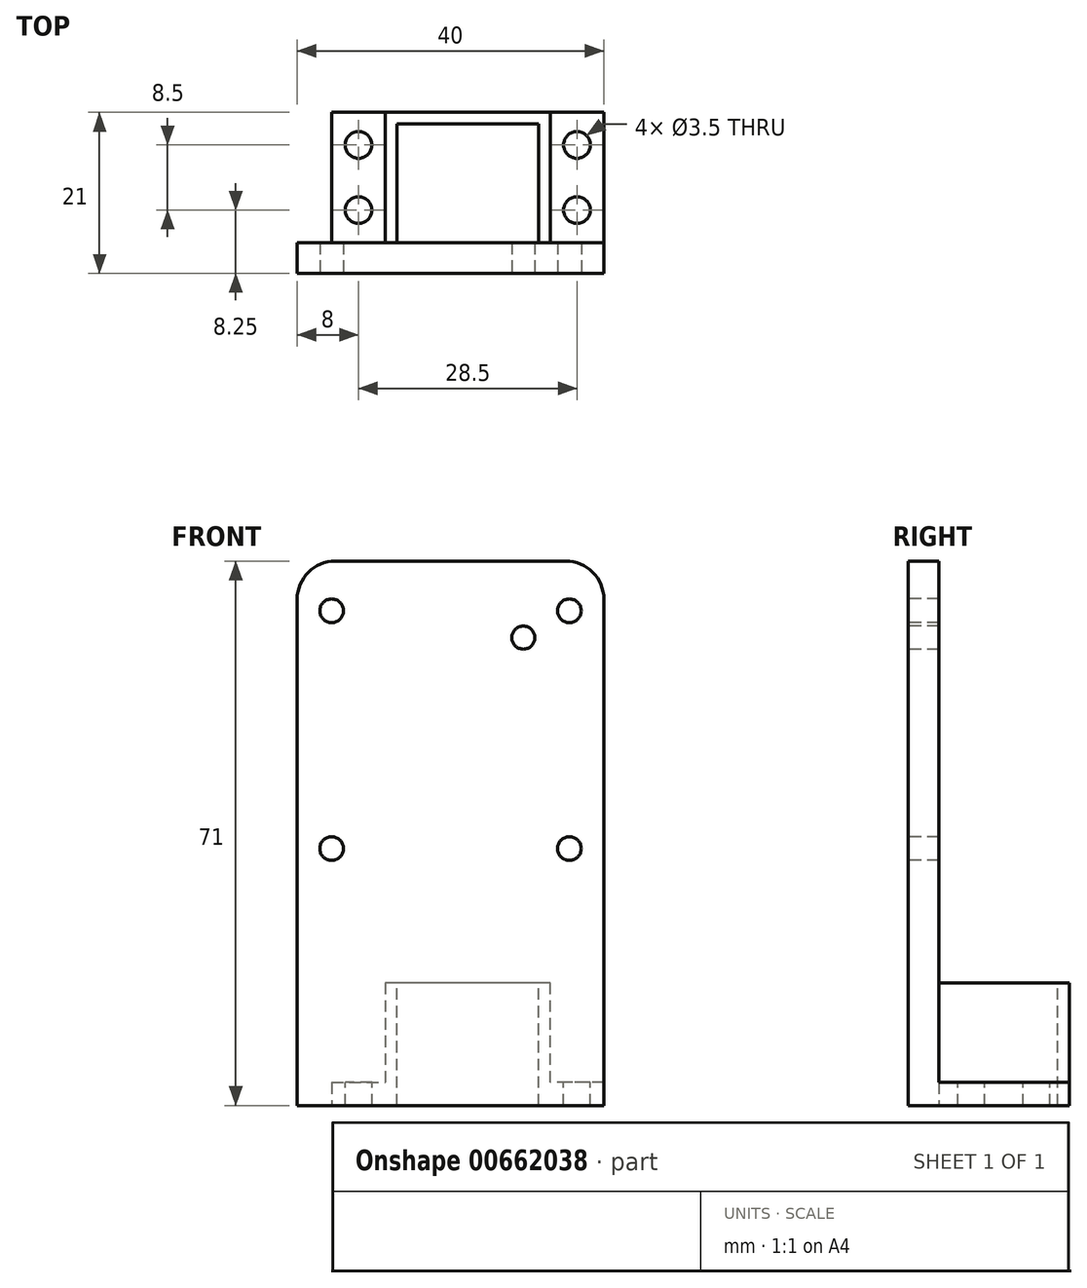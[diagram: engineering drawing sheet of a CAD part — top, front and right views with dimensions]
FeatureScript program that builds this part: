
annotation { "Feature Type Name" : "Feature", "Feature Type Description" : "" }
export const myFeature = defineFeature(function(context is Context, id is Id, definition is map)
    precondition{}
    {
        {
            var Q0;
            Q0=qCreatedBy(makeId("Front.planeOp"),FACE);
            var sketch = newSketch(context, id + "F0", { "sketchPlane" : qUnion([Q0])});
            skLineSegment(sketch, "E0.bottom", {"start": v(-20, 35.5) * mm, "end": v(20, 35.5) * mm});
            skLineSegment(sketch, "E0.top", {"start": v(-20, -35.5) * mm, "end": v(20, -35.5) * mm});
            skLineSegment(sketch, "E0.left", {"start": v(-20, 35.5) * mm, "end": v(-20, -35.5) * mm});
            skLineSegment(sketch, "E0.right", {"start": v(20, 35.5) * mm, "end": v(20, -35.5) * mm});
            skPoint(sketch, "E0.middle", {"position": v(0, 0) * mm});
            skSolve(sketch);
        }
        {
            var Q0;
            Q0 = qSketchRegion(id + "F0", true);
            extrude(context, id + "F1", {"entities" : qUnion([Q0]), "depth" : 4 * mm, "offsetDistance" : 25 * mm});
        }
        {
            var Q0;
            Q0=makeQuery(id+"F1.opExtrude","CAP_FACE",FACE,{"disambiguationData":[OSD([sQuery(id+"F0.wireOp",EDGE,"E0.bottom"),sQuery(id+"F0.wireOp",EDGE,"E0.top"),sQuery(id+"F0.wireOp",EDGE,"E0.left"),sQuery(id+"F0.wireOp",EDGE,"E0.right")])],"isStart":false});
            var sketch = newSketch(context, id + "F2", { "sketchPlane" : qUnion([Q0])});
            skLineSegment(sketch, "E1", {"start": v(-20, 35.5) * mm, "end": v(-20, 30.5) * mm});
            skLineSegment(sketch, "E2", {"start": v(0, 0) * mm, "end": v(0, 29) * mm});
            skLineSegment(sketch, "E3", {"start": v(0, 29) * mm, "end": v(-15.5, 29) * mm});
            skLineSegment(sketch, "E4", {"start": v(0, 29) * mm, "end": v(15.5, 29) * mm});
            skCircle(sketch, "E5", {"center": v(-15.5, 29) * mm, "radius": 1.55 * mm});
            skCircle(sketch, "E6", {"center": v(15.5, 29) * mm, "radius": 1.55 * mm});
            skLineSegment(sketch, "E7", {"start": v(-15.5, 29) * mm, "end": v(-15.5, 35.5) * mm});
            skLineSegment(sketch, "E8", {"start": v(-15.5, 29) * mm, "end": v(-15.5, -2) * mm});
            skLineSegment(sketch, "E9", {"start": v(-15.5, -2) * mm, "end": v(15.5, -2) * mm});
            skCircle(sketch, "E10", {"center": v(-15.5, -2) * mm, "radius": 1.55 * mm});
            skCircle(sketch, "E11", {"center": v(15.5, -2) * mm, "radius": 1.55 * mm});
            skSolve(sketch);
        }
        {
            var Q0;
            Q0 = qSketchRegion(id + "F2", true);
            extrude(context, id + "F3", {"entities" : qUnion([Q0]), "operationType" : NewBodyOperationType.REMOVE, "oppositeDirection" : true, "depth" : 25 * mm, "offsetDistance" : 25 * mm});
        }
        {
            var Q0;
            Q0=makeQuery(id+"F1.opExtrude","CAP_FACE",FACE,{"disambiguationData":[OSD([sQuery(id+"F0.wireOp",EDGE,"E0.bottom"),sQuery(id+"F0.wireOp",EDGE,"E0.top"),sQuery(id+"F0.wireOp",EDGE,"E0.left"),sQuery(id+"F0.wireOp",EDGE,"E0.right")])],"isStart":true});
            var sketch = newSketch(context, id + "F4", { "sketchPlane" : qUnion([Q0])});
            skLineSegment(sketch, "E12", {"start": v(-20, -35.5) * mm, "end": v(-13, -35.5) * mm});
            skLineSegment(sketch, "E13", {"start": v(-13, -35.5) * mm, "end": v(8.5, -35.5) * mm});
            skLineSegment(sketch, "E14", {"start": v(-13, -35.5) * mm, "end": v(-13, -19.5) * mm});
            skLineSegment(sketch, "E15", {"start": v(-13, -19.5) * mm, "end": v(8.5, -19.5) * mm});
            skLineSegment(sketch, "E16", {"start": v(8.5, -19.5) * mm, "end": v(8.5, -35.5) * mm});
            skSolve(sketch);
        }
        {
            var Q0;
            Q0 = qSketchRegion(id + "F4", true);
            extrude(context, id + "F5", {"entities" : qUnion([Q0]), "operationType" : NewBodyOperationType.ADD, "depth" : 17 * mm, "offsetDistance" : 25 * mm});
        }
        {
            var Q0;
            Q0=makeQuery(id+"F5.opExtrude","SWEPT_FACE",FACE,{"disambiguationData":[OSD([sQuery(id+"F4.wireOp",EDGE,"E15")])]});
            var sketch = newSketch(context, id + "F6", { "sketchPlane" : qUnion([Q0])});
            skLineSegment(sketch, "E17", {"start": v(13, 0) * mm, "end": v(11.5, 0) * mm});
            skLineSegment(sketch, "E18", {"start": v(11.5, 0) * mm, "end": v(11.5, 17) * mm});
            skLineSegment(sketch, "E19", {"start": v(-8.5, 0) * mm, "end": v(-7, 0) * mm});
            skLineSegment(sketch, "E20", {"start": v(-7, 0) * mm, "end": v(-7, 17) * mm});
            skLineSegment(sketch, "E21", {"start": v(13, 17) * mm, "end": v(13, 15.5) * mm});
            skLineSegment(sketch, "E22", {"start": v(13, 15.5) * mm, "end": v(-8.5, 15.5) * mm});
            skSolve(sketch);
        }
        {
            var Q0;
            {var subQ0=sQuery(id+"F6.wireOp",EDGE,"E18");var subQ3=sQuery(id+"F6.wireOp",EDGE,"E22");var subQ4=makeQuery(id+"F6.imprint","INTERSECT",VERTEX,{"derivedFrom":[subQ0,subQ3]});Q0=makeQuery(id+"F6.imprint","IMPRINT",FACE,{"disambiguationData":[TD([[makeQuery(id+"F6.imprint","IMPRINT",EDGE,{"disambiguationData":[TD([[subQ4,-1.0]])],"derivedFrom":subQ3}),1.0]])]});}
            extrude(context, id + "F7", {"entities" : qUnion([Q0]), "operationType" : NewBodyOperationType.REMOVE, "oppositeDirection" : true, "depth" : 25 * mm, "offsetDistance" : 25 * mm});
        }
        {
            var Q0;
            Q0=makeQuery(id+"F5.opExtrude","SWEPT_FACE",FACE,{"disambiguationData":[OSD([sQuery(id+"F4.wireOp",EDGE,"E14")])]});
            var sketch = newSketch(context, id + "F8", { "sketchPlane" : qUnion([Q0])});
            skLineSegment(sketch, "E23.bottom", {"start": v(0, -35.5) * mm, "end": v(17, -35.5) * mm});
            skLineSegment(sketch, "E23.top", {"start": v(0, -32.5) * mm, "end": v(17, -32.5) * mm});
            skLineSegment(sketch, "E23.left", {"start": v(0, -35.5) * mm, "end": v(0, -32.5) * mm});
            skLineSegment(sketch, "E23.right", {"start": v(17, -35.5) * mm, "end": v(17, -32.5) * mm});
            skSolve(sketch);
        }
        {
            var Q0;
            Q0 = qSketchRegion(id + "F8", true);
            extrude(context, id + "F9", {"entities" : qUnion([Q0]), "operationType" : NewBodyOperationType.ADD, "depth" : 7 * mm, "offsetDistance" : 25 * mm});
        }
        {
            var Q0;
            Q0=makeQuery(id+"F5.opExtrude","SWEPT_FACE",FACE,{"disambiguationData":[OSD([sQuery(id+"F4.wireOp",EDGE,"E16")])]});
            var sketch = newSketch(context, id + "F10", { "sketchPlane" : qUnion([Q0])});
            skLineSegment(sketch, "E24.bottom", {"start": v(0, -35.5) * mm, "end": v(-17, -35.5) * mm});
            skLineSegment(sketch, "E24.top", {"start": v(0, -32.5) * mm, "end": v(-17, -32.5) * mm});
            skLineSegment(sketch, "E24.left", {"start": v(0, -35.5) * mm, "end": v(0, -32.5) * mm});
            skLineSegment(sketch, "E24.right", {"start": v(-17, -35.5) * mm, "end": v(-17, -32.5) * mm});
            skSolve(sketch);
        }
        {
            var Q0;
            Q0 = qSketchRegion(id + "F10", true);
            extrude(context, id + "F11", {"entities" : qUnion([Q0]), "operationType" : NewBodyOperationType.ADD, "depth" : 7 * mm, "offsetDistance" : 25 * mm});
        }
        {
            var Q0;
            Q0=makeQuery(id+"F11.opExtrude","SWEPT_FACE",FACE,{"disambiguationData":[OSD([sQuery(id+"F10.wireOp",EDGE,"E24.top")])]});
            var sketch = newSketch(context, id + "F12", { "sketchPlane" : qUnion([Q0])});
            skLineSegment(sketch, "E25", {"start": v(-12, 0) * mm, "end": v(-12, 8.5) * mm});
            skLineSegment(sketch, "E26", {"start": v(-12, 8.5) * mm, "end": v(-12, 17) * mm});
            skCircle(sketch, "E27", {"center": v(-12, 12.75) * mm, "radius": 1.75 * mm});
            skCircle(sketch, "E28", {"center": v(-12, 4.25) * mm, "radius": 1.75 * mm});
            skSolve(sketch);
        }
        {
            var Q0;
            {var subQ0=sQuery(id+"F12.wireOp",EDGE,"E27");var subQ1=sQuery(id+"F12.wireOp",EDGE,"E26");var subQ2=makeQuery(id+"F12.imprint","INTERSECT",VERTEX,{"disambiguationData":[OD(0.0)],"derivedFrom":[subQ1,subQ0]});Q0=makeQuery(id+"F12.imprint","IMPRINT",FACE,{"disambiguationData":[TD([[makeQuery(id+"F12.imprint","IMPRINT",EDGE,{"disambiguationData":[TD([[subQ2,-1.0]])],"derivedFrom":subQ1}),-1.0]])]});}
            var Q1;
            {var subQ0=sQuery(id+"F12.wireOp",EDGE,"E27");var subQ1=sQuery(id+"F12.wireOp",EDGE,"E26");var subQ2=makeQuery(id+"F12.imprint","INTERSECT",VERTEX,{"disambiguationData":[OD(0.0)],"derivedFrom":[subQ1,subQ0]});Q1=makeQuery(id+"F12.imprint","IMPRINT",FACE,{"disambiguationData":[TD([[makeQuery(id+"F12.imprint","IMPRINT",EDGE,{"disambiguationData":[TD([[subQ2,-1.0]])],"derivedFrom":subQ1}),1.0]])]});}
            var Q2;
            {var subQ0=sQuery(id+"F12.wireOp",EDGE,"E28");var subQ1=sQuery(id+"F12.wireOp",EDGE,"E25");var subQ2=makeQuery(id+"F12.imprint","INTERSECT",VERTEX,{"disambiguationData":[OD(0.0)],"derivedFrom":[subQ1,subQ0]});Q2=makeQuery(id+"F12.imprint","IMPRINT",FACE,{"disambiguationData":[TD([[makeQuery(id+"F12.imprint","IMPRINT",EDGE,{"disambiguationData":[TD([[subQ2,-1.0]])],"derivedFrom":subQ1}),1.0]])]});}
            var Q3;
            {var subQ0=sQuery(id+"F12.wireOp",EDGE,"E28");var subQ1=sQuery(id+"F12.wireOp",EDGE,"E25");var subQ2=makeQuery(id+"F12.imprint","INTERSECT",VERTEX,{"disambiguationData":[OD(0.0)],"derivedFrom":[subQ1,subQ0]});Q3=makeQuery(id+"F12.imprint","IMPRINT",FACE,{"disambiguationData":[TD([[makeQuery(id+"F12.imprint","IMPRINT",EDGE,{"disambiguationData":[TD([[subQ2,-1.0]])],"derivedFrom":subQ1}),-1.0]])]});}
            extrude(context, id + "F13", {"entities" : qUnion([Q0, Q1, Q2, Q3]), "operationType" : NewBodyOperationType.REMOVE, "oppositeDirection" : true, "depth" : 25 * mm, "offsetDistance" : 25 * mm});
        }
        {
            var Q0;
            Q0=makeQuery(id+"F9.opExtrude","SWEPT_FACE",FACE,{"disambiguationData":[OSD([sQuery(id+"F8.wireOp",EDGE,"E23.top")])]});
            var sketch = newSketch(context, id + "F14", { "sketchPlane" : qUnion([Q0])});
            skLineSegment(sketch, "E29", {"start": v(16.5, 17) * mm, "end": v(16.5, 8.5) * mm});
            skLineSegment(sketch, "E30", {"start": v(16.5, 8.5) * mm, "end": v(16.5, 0) * mm});
            skCircle(sketch, "E31", {"center": v(16.5, 12.75) * mm, "radius": 1.75 * mm});
            skCircle(sketch, "E32", {"center": v(16.5, 4.25) * mm, "radius": 1.75 * mm});
            skSolve(sketch);
        }
        {
            var Q0;
            Q0 = qSketchRegion(id + "F14", true);
            extrude(context, id + "F15", {"entities" : qUnion([Q0]), "operationType" : NewBodyOperationType.REMOVE, "oppositeDirection" : true, "depth" : 25 * mm, "offsetDistance" : 25 * mm});
        }
        {
            var Q0;
            Q0=makeQuery(id+"F1.opExtrude","CAP_FACE",FACE,{"disambiguationData":[OSD([sQuery(id+"F0.wireOp",EDGE,"E0.bottom"),sQuery(id+"F0.wireOp",EDGE,"E0.top"),sQuery(id+"F0.wireOp",EDGE,"E0.left"),sQuery(id+"F0.wireOp",EDGE,"E0.right")])],"isStart":false});
            var sketch = newSketch(context, id + "F16", { "sketchPlane" : qUnion([Q0])});
            skLineSegment(sketch, "E33.bottom", {"start": v(-20, -35.5) * mm, "end": v(-11, -35.5) * mm});
            skLineSegment(sketch, "E33.top", {"start": v(-20, -25.5) * mm, "end": v(-11, -25.5) * mm});
            skLineSegment(sketch, "E33.left", {"start": v(-20, -35.5) * mm, "end": v(-20, -25.5) * mm});
            skLineSegment(sketch, "E33.right", {"start": v(-11, -35.5) * mm, "end": v(-11, -25.5) * mm});
            skLineSegment(sketch, "E34", {"start": v(-15.5, -35.5) * mm, "end": v(-15.5, -30.5) * mm});
            skPoint(sketch, "E34.endSnap0", {"position": v(-20, -30.5) * mm});
            skCircle(sketch, "E35", {"center": v(-15.5, -30.5) * mm, "radius": 1.75 * mm});
            skSolve(sketch);
        }
        {
            var Q0;
            Q0 = qSketchRegion(id + "F16", true);
            extrude(context, id + "F17", {"entities" : qUnion([Q0]), "operationType" : NewBodyOperationType.ADD, "depth" : 10 * mm, "offsetDistance" : 25 * mm});
        }
        {
            var Q0;
            Q0=makeQuery(id+"F17.boolean.opBoolean","SPLIT",FACE,{"disambiguationData":[TD([makeQuery(id+"F17.opExtrude","SWEPT_FACE",FACE,{"disambiguationData":[OSD([sQuery(id+"F16.wireOp",EDGE,"E35")])]})])],"derivedFrom":makeQuery(id+"F1.opExtrude","CAP_FACE",FACE,{"disambiguationData":[OSD([sQuery(id+"F0.wireOp",EDGE,"E0.bottom"),sQuery(id+"F0.wireOp",EDGE,"E0.top"),sQuery(id+"F0.wireOp",EDGE,"E0.left"),sQuery(id+"F0.wireOp",EDGE,"E0.right")])],"isStart":false})});
            extrude(context, id + "F18", {"entities" : qUnion([Q0]), "operationType" : NewBodyOperationType.REMOVE, "oppositeDirection" : true, "depth" : 25 * mm, "offsetDistance" : 25 * mm});
        }
        {
            var Q0;
            Q0=makeQuery(id+"F7.boolean.opBoolean","MERGE",FACE,{"derivedFrom":[makeQuery(id+"F1.opExtrude","CAP_FACE",FACE,{"disambiguationData":[OSD([sQuery(id+"F0.wireOp",EDGE,"E0.bottom"),sQuery(id+"F0.wireOp",EDGE,"E0.top"),sQuery(id+"F0.wireOp",EDGE,"E0.left"),sQuery(id+"F0.wireOp",EDGE,"E0.right")])],"isStart":true}),makeQuery(id+"F7.opExtrude","SWEPT_FACE",FACE,{"disambiguationData":[OSD([sQuery(id+"F4.wireOp",EDGE,"E15")])]})]});
            var sketch = newSketch(context, id + "F19", { "sketchPlane" : qUnion([Q0])});
            skLineSegment(sketch, "E36.bottom", {"start": v(12.75, -27.5) * mm, "end": v(18.25, -27.5) * mm});
            skLineSegment(sketch, "E36.top", {"start": v(12.75, -33.5) * mm, "end": v(18.25, -33.5) * mm});
            skLineSegment(sketch, "E36.left", {"start": v(12.75, -27.5) * mm, "end": v(12.75, -33.5) * mm});
            skLineSegment(sketch, "E36.right", {"start": v(18.25, -27.5) * mm, "end": v(18.25, -33.5) * mm});
            skPoint(sketch, "E36.middle", {"position": v(15.5, -30.5) * mm});
            skSolve(sketch);
        }
        {
            var Q0;
            Q0=makeQuery(id+"F1.opExtrude","SWEPT_EDGE",EDGE,{"disambiguationData":[OSD([sQuery(id+"F0.wireOp",EDGE,"E0.bottom"),sQuery(id+"F0.wireOp",EDGE,"E0.left")])]});
            var Q1;
            Q1=makeQuery(id+"F1.opExtrude","SWEPT_EDGE",EDGE,{"disambiguationData":[OSD([sQuery(id+"F0.wireOp",EDGE,"E0.bottom"),sQuery(id+"F0.wireOp",EDGE,"E0.right")])]});
            fillet(context, id + "F20", {"entities" : qUnion([Q0, Q1]), "radius" : 5 * mm, "tangentPropagation" : true, "allowEdgeOverflow" : false});
        }
        {
            var Q0;
            Q0=makeQuery(id+"F17.opExtrude","CAP_FACE",FACE,{"disambiguationData":[OSD([sQuery(id+"F16.wireOp",EDGE,"E33.bottom"),sQuery(id+"F16.wireOp",EDGE,"E33.top"),sQuery(id+"F16.wireOp",EDGE,"E33.left"),sQuery(id+"F16.wireOp",EDGE,"E33.right"),sQuery(id+"F16.wireOp",EDGE,"E35")])],"isStart":false});
            extrude(context, id + "F21", {"entities" : qUnion([Q0]), "operationType" : NewBodyOperationType.REMOVE, "oppositeDirection" : true, "depth" : 10 * mm, "offsetDistance" : 25 * mm});
        }
        {
            var Q0;
            {var subQ0=sQuery(id+"F16.wireOp",EDGE,"E33.right");var subQ1=sQuery(id+"F16.wireOp",EDGE,"E33.left");var subQ2=sQuery(id+"F16.wireOp",EDGE,"E33.top");var subQ3=sQuery(id+"F16.wireOp",EDGE,"E33.bottom");var subQ4=sQuery(id+"F0.wireOp",EDGE,"E0.bottom");var subQ6=sQuery(id+"F0.wireOp",EDGE,"E0.right");var subQ7=sQuery(id+"F0.wireOp",EDGE,"E0.top");var subQ8=sQuery(id+"F0.wireOp",EDGE,"E0.left");Q0=makeQuery(id+"F21.boolean.opBoolean","MERGE",FACE,{"derivedFrom":[makeQuery(id+"F17.boolean.opBoolean","SPLIT",FACE,{"disambiguationData":[TD([makeQuery(id+"F1.opExtrude","SWEPT_FACE",FACE,{"disambiguationData":[OSD([subQ4])]})])],"derivedFrom":makeQuery(id+"F1.opExtrude","CAP_FACE",FACE,{"disambiguationData":[OSD([subQ4,subQ7,subQ8,subQ6])],"isStart":false})})],"fromTools":[makeQuery(id+"F21.opExtrude","CAP_FACE",FACE,{"disambiguationData":[OSD([subQ3,subQ2,subQ1,subQ0,sQuery(id+"F16.wireOp",EDGE,"E35")])],"isStart":false})]});}
            var sketch = newSketch(context, id + "F22", { "sketchPlane" : qUnion([Q0])});
            skCircle(sketch, "E37", {"center": v(-15.5, -30.5) * mm, "radius": 2 * mm});
            skSolve(sketch);
        }
        {
            var Q0;
            Q0 = qSketchRegion(id + "F22", true);
            extrude(context, id + "F23", {"entities" : qUnion([Q0]), "operationType" : NewBodyOperationType.ADD, "oppositeDirection" : true, "depth" : 4 * mm, "offsetDistance" : 25 * mm});
        }
        {
            var Q0;
            {var subQ0=sQuery(id+"F16.wireOp",EDGE,"E33.right");var subQ1=sQuery(id+"F16.wireOp",EDGE,"E33.left");var subQ2=sQuery(id+"F16.wireOp",EDGE,"E33.top");var subQ3=sQuery(id+"F16.wireOp",EDGE,"E33.bottom");var subQ4=sQuery(id+"F0.wireOp",EDGE,"E0.bottom");var subQ6=sQuery(id+"F0.wireOp",EDGE,"E0.right");var subQ7=sQuery(id+"F0.wireOp",EDGE,"E0.top");var subQ8=sQuery(id+"F0.wireOp",EDGE,"E0.left");Q0=makeQuery(id+"F23.boolean.opBoolean","MERGE",FACE,{"derivedFrom":[makeQuery(id+"F21.boolean.opBoolean","MERGE",FACE,{"derivedFrom":[makeQuery(id+"F17.boolean.opBoolean","SPLIT",FACE,{"disambiguationData":[TD([makeQuery(id+"F1.opExtrude","SWEPT_FACE",FACE,{"disambiguationData":[OSD([subQ4])]})])],"derivedFrom":makeQuery(id+"F1.opExtrude","CAP_FACE",FACE,{"disambiguationData":[OSD([subQ4,subQ7,subQ8,subQ6])],"isStart":false})})],"fromTools":[makeQuery(id+"F21.opExtrude","CAP_FACE",FACE,{"disambiguationData":[OSD([subQ3,subQ2,subQ1,subQ0,sQuery(id+"F16.wireOp",EDGE,"E35")])],"isStart":false})]}),makeQuery(id+"F23.opExtrude","CAP_FACE",FACE,{"disambiguationData":[OSD([sQuery(id+"F22.wireOp",EDGE,"E37")])],"isStart":true})]});}
            var sketch = newSketch(context, id + "F24", { "sketchPlane" : qUnion([Q0])});
            skLineSegment(sketch, "E38", {"start": v(20, -35.5) * mm, "end": v(9.5, -35.5) * mm});
            skLineSegment(sketch, "E39", {"start": v(9.5, -35.5) * mm, "end": v(9.5, 25.5) * mm});
            skCircle(sketch, "E40", {"center": v(9.5, 25.5) * mm, "radius": 1.5 * mm});
            skSolve(sketch);
        }
        {
            var Q0;
            Q0 = qSketchRegion(id + "F24", true);
            extrude(context, id + "F25", {"entities" : qUnion([Q0]), "operationType" : NewBodyOperationType.REMOVE, "oppositeDirection" : true, "depth" : 25 * mm, "offsetDistance" : 25 * mm});
        }
    });
